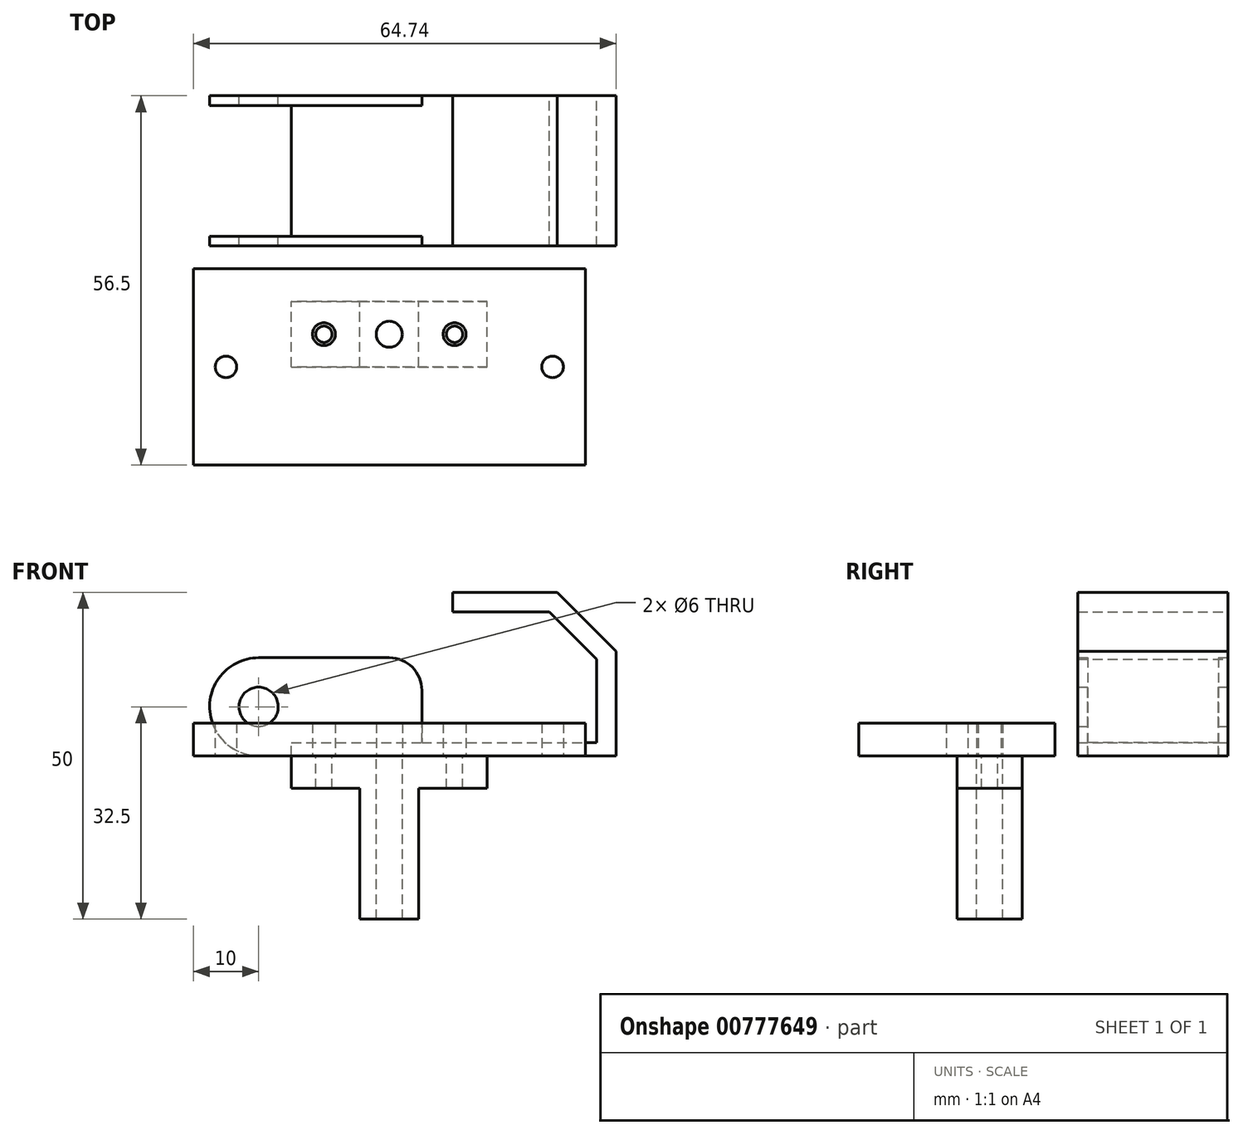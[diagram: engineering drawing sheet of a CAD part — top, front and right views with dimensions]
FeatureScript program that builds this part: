
annotation { "Feature Type Name" : "Feature", "Feature Type Description" : "" }
export const myFeature = defineFeature(function(context is Context, id is Id, definition is map)
    precondition{}
    {
        {
            var Q0;
            Q0=qCreatedBy(makeId("Front.planeOp"),FACE);
            cPlane(context, id + "F0", {"entities" : qUnion([Q0]), "cplaneType" : CPlaneType.OFFSET, "offset" : 25 * mm, "oppositeDirection" : true, "width" : 150 * mm, "height" : 150 * mm});
        }
        {
            var Q0;
            Q0=qCreatedBy(id+"F0.planeOp",FACE);
            var sketch = newSketch(context, id + "F1", { "sketchPlane" : qUnion([Q0])});
            skLineSegment(sketch, "E0", {"start": v(34.74, 0) * mm, "end": v(-20, 0) * mm});
            skLineSegment(sketch, "E1", {"start": v(-20, 0) * mm, "end": v(-20, 15) * mm, "construction": true});
            skLineSegment(sketch, "E2", {"start": v(-20, 15) * mm, "end": v(0, 15) * mm});
            skLineSegment(sketch, "E3", {"start": v(5, 10) * mm, "end": v(5, 2) * mm});
            skLineSegment(sketch, "E4", {"start": v(5, 2) * mm, "end": v(31.74, 2) * mm});
            skLineSegment(sketch, "E5", {"start": v(31.74, 2) * mm, "end": v(31.74, 14.76) * mm});
            skLineSegment(sketch, "E6", {"start": v(31.74, 14.76) * mm, "end": v(24.5, 22) * mm});
            skLineSegment(sketch, "E7", {"start": v(24.5, 22) * mm, "end": v(9.74, 22) * mm});
            skLineSegment(sketch, "E8", {"start": v(9.74, 22) * mm, "end": v(9.74, 25) * mm});
            skLineSegment(sketch, "E9", {"start": v(9.74, 25) * mm, "end": v(25.74, 25) * mm});
            skLineSegment(sketch, "E10", {"start": v(25.74, 25) * mm, "end": v(34.74, 16) * mm});
            skLineSegment(sketch, "E11", {"start": v(34.74, 16) * mm, "end": v(34.74, 0) * mm});
            skArc(sketch, "E12", {"start": v(-20, 15) * mm, "mid": v(-27.5, 7.5) * mm, "end": v(-20, 0) * mm});
            skCircle(sketch, "E13", {"center": v(-20, 7.5) * mm, "radius": 3 * mm});
            skLineSegment(sketch, "E14", {"start": v(25.74, 25) * mm, "end": v(23.62, 22.88) * mm, "construction": true});
            skLineSegment(sketch, "E15", {"start": v(31.74, 2) * mm, "end": v(34.74, 2) * mm, "construction": true});
            skPoint(sketch, "E16.visualSharp", {"position": v(5, 15) * mm});
            skArc(sketch, "E16.filletArc", {"start": v(5, 10) * mm, "mid": v(3.54, 13.54) * mm, "end": v(0, 15) * mm});
            skSolve(sketch);
        }
        {
            var Q0;
            Q0=makeQuery(id+"F1.imprint","IMPRINT",FACE,{"disambiguationData":[TD([[makeQuery(id+"F1.imprint","IMPRINT",EDGE,{"derivedFrom":sQuery(id+"F1.wireOp",EDGE,"E0")}),-1.0]])]});
            extrude(context, id + "F2", {"entities" : qUnion([Q0]), "depth" : 23 * mm, "symmetric" : true});
        }
        {
            var Q0;
            Q0=makeQuery(id+"F2.opExtrude","SWEPT_FACE",FACE,{"disambiguationData":[OSD([sQuery(id+"F1.wireOp",EDGE,"E2")])]});
            var sketch = newSketch(context, id + "F3", { "sketchPlane" : qUnion([Q0])});
            skLineSegment(sketch, "E17.bottom", {"start": v(-45, 35) * mm, "end": v(-15, 35) * mm});
            skLineSegment(sketch, "E17.top", {"start": v(-45, 15) * mm, "end": v(-15, 15) * mm});
            skLineSegment(sketch, "E17.left", {"start": v(-45, 35) * mm, "end": v(-45, 15) * mm});
            skLineSegment(sketch, "E17.right", {"start": v(-15, 35) * mm, "end": v(-15, 15) * mm});
            skSolve(sketch);
        }
        {
            var Q0;
            Q0 = qSketchRegion(id + "F3", true);
            extrude(context, id + "F4", {"entities" : qUnion([Q0]), "operationType" : NewBodyOperationType.REMOVE, "endBound" : BoundingType.THROUGH_ALL, "oppositeDirection" : true, "depth" : 25 * mm});
        }
        {
            var Q0;
            Q0=makeQuery(id+"F2.opExtrude","SWEPT_FACE",FACE,{"disambiguationData":[OSD([sQuery(id+"F1.wireOp",EDGE,"E3")])]});
            var sketch = newSketch(context, id + "F5", { "sketchPlane" : qUnion([Q0])});
            skLineSegment(sketch, "E18.bottom", {"start": v(15, 2) * mm, "end": v(35, 2) * mm});
            skLineSegment(sketch, "E18.top", {"start": v(15, 22) * mm, "end": v(35, 22) * mm});
            skLineSegment(sketch, "E18.left", {"start": v(15, 2) * mm, "end": v(15, 22) * mm});
            skLineSegment(sketch, "E18.right", {"start": v(35, 2) * mm, "end": v(35, 22) * mm});
            skSolve(sketch);
        }
        {
            var Q0;
            Q0 = qSketchRegion(id + "F5", true);
            extrude(context, id + "F6", {"entities" : qUnion([Q0]), "operationType" : NewBodyOperationType.REMOVE, "endBound" : BoundingType.THROUGH_ALL, "oppositeDirection" : true, "depth" : 25 * mm});
        }
        {
            var Q0;
            Q0=qCreatedBy(makeId("Top.planeOp"),FACE);
            var sketch = newSketch(context, id + "F7", { "sketchPlane" : qUnion([Q0])});
            skCircle(sketch, "E19", {"center": v(0, 0) * mm, "radius": 2 * mm});
            skCircle(sketch, "E20", {"center": v(-25, -5) * mm, "radius": 1.65 * mm});
            skCircle(sketch, "E21", {"center": v(25, -5) * mm, "radius": 1.65 * mm});
            skLineSegment(sketch, "E22.bottom", {"start": v(-30, 10) * mm, "end": v(30, 10) * mm});
            skLineSegment(sketch, "E22.top", {"start": v(-30, -20) * mm, "end": v(30, -20) * mm});
            skLineSegment(sketch, "E22.left", {"start": v(-30, 10) * mm, "end": v(-30, -20) * mm});
            skLineSegment(sketch, "E22.right", {"start": v(30, 10) * mm, "end": v(30, -20) * mm});
            skCircle(sketch, "E23", {"center": v(-10, 0) * mm, "radius": 1.75 * mm});
            skCircle(sketch, "E24.MirrorC", {"center": v(10, 0) * mm, "radius": 1.75 * mm});
            skSolve(sketch);
        }
        {
            var Q0;
            Q0 = qSketchRegion(id + "F7", true);
            extrude(context, id + "F8", {"entities" : qUnion([Q0]), "depth" : 5 * mm});
        }
        {
            var Q0;
            Q0=qCreatedBy(makeId("Front.planeOp"),FACE);
            var sketch = newSketch(context, id + "F9", { "sketchPlane" : qUnion([Q0])});
            skLineSegment(sketch, "E25", {"start": v(15, 0) * mm, "end": v(-15, 0) * mm});
            skLineSegment(sketch, "E26", {"start": v(-15, 0) * mm, "end": v(-15, -5) * mm});
            skLineSegment(sketch, "E27", {"start": v(-15, -5) * mm, "end": v(-4.5, -5) * mm});
            skLineSegment(sketch, "E28", {"start": v(-4.5, -5) * mm, "end": v(-4.5, -25) * mm});
            skLineSegment(sketch, "E29", {"start": v(-4.5, -25) * mm, "end": v(4.5, -25) * mm});
            skLineSegment(sketch, "E30", {"start": v(4.5, -25) * mm, "end": v(4.5, -5) * mm});
            skLineSegment(sketch, "E31", {"start": v(4.5, -5) * mm, "end": v(15, -5) * mm});
            skLineSegment(sketch, "E32", {"start": v(15, -5) * mm, "end": v(15, 0) * mm});
            skSolve(sketch);
        }
        {
            var Q0;
            Q0=makeQuery(id+"F9.imprint","IMPRINT",FACE,{"disambiguationData":[TD([[makeQuery(id+"F9.imprint","IMPRINT",EDGE,{"derivedFrom":sQuery(id+"F9.wireOp",EDGE,"E25")}),1.0]])]});
            extrude(context, id + "F10", {"entities" : qUnion([Q0]), "depth" : 10 * mm, "symmetric" : true});
        }
        {
            var Q0;
            Q0=sQuery(id+"F7.wireOp",VERTEX,"E19.center");
            var Q1;
            Q1=makeQuery(id+"F10.opExtrude","SWEPT_BODY",BODY,{"disambiguationData":[OSD([sQuery(id+"F9.wireOp",EDGE,"E25"),sQuery(id+"F9.wireOp",EDGE,"E26"),sQuery(id+"F9.wireOp",EDGE,"E27"),sQuery(id+"F9.wireOp",EDGE,"E28"),sQuery(id+"F9.wireOp",EDGE,"E29"),sQuery(id+"F9.wireOp",EDGE,"E30"),sQuery(id+"F9.wireOp",EDGE,"E31"),sQuery(id+"F9.wireOp",EDGE,"E32")])]});
            hole(context, id + "F11", {"style" : HoleStyle.SIMPLE, "endStyle" : HoleEndStyle.THROUGH, "holeDiameter" : 4 * mm, "isTappedThrough" : true, "tappedDepth" : 12 * mm, "tapClearance" : 3, "locations" : qUnion([Q0]), "scope" : qUnion([Q1])});
        }
        {
            var Q0;
            Q0=sQuery(id+"F7.wireOp",VERTEX,"E23.center");
            var Q1;
            Q1=sQuery(id+"F7.wireOp",VERTEX,"E24.MirrorC.center");
            var Q2;
            Q2=makeQuery(id+"F10.opExtrude","SWEPT_BODY",BODY,{"disambiguationData":[OSD([sQuery(id+"F9.wireOp",EDGE,"E25"),sQuery(id+"F9.wireOp",EDGE,"E26"),sQuery(id+"F9.wireOp",EDGE,"E27"),sQuery(id+"F9.wireOp",EDGE,"E28"),sQuery(id+"F9.wireOp",EDGE,"E29"),sQuery(id+"F9.wireOp",EDGE,"E30"),sQuery(id+"F9.wireOp",EDGE,"E31"),sQuery(id+"F9.wireOp",EDGE,"E32")])]});
            hole(context, id + "F12", {"style" : HoleStyle.SIMPLE, "endStyle" : HoleEndStyle.THROUGH, "standardTappedOrClearance" : lookupTablePath({ "standard" : "ISO", "engagement" : "75%", "pitch" : "0.5 mm", "size" : "M3", "type" : "Tapped" }), "standardBlindInLast" : lookupTablePath({ "standard" : "ISO", "engagement" : "75%", "pitch" : "0.5 mm", "size" : "M3", "type" : "Tapped" }), "holeDiameter" : 2.5 * mm, "showTappedDepth" : true, "isTappedThrough" : true, "tappedDepth" : 12 * mm, "tapClearance" : 3, "locations" : qUnion([Q0, Q1]), "scope" : qUnion([Q2]), "majorDiameter" : 3 * mm});
        }
    });
